# Revit family: Guardrail_Kattsafe_TopMount
name_source: partatom
category: Specialty Equipment
units: mm (PartAtom-declared; Revit-internal decimal feet)

## family parameters
Cut with Voids When Loaded = No
Enable Cutting in Views = No
Maintain Annotation Orientation = No
OmniClass Number = 23.17.25.11
Part Type = Normal
Room Calculation Point = No
Round Connector Dimension = Use Diameter
Shared = No

## types (1)
- Type 1
    Assembly Code = E1090100
    Default Elevation = 0 mm  [stored 0 ft]
    Description = Kattsafe guardrail systems are the preferred method of safe access across roofs and areas close to a fall edge. The system requires no specialist PPE, personnel or training to safely prevent a fall with a walkway to designate a safe path of access across the roof surface.
    Export Type to IFC As = IfcRailing
    GuardrailHeight = 1000 mm  [stored 3.28084 ft]
    HandrailAngledOffsetHeight = -57 mm
    HandrailClosureAngledOffsetHeight = -532 mm
    IfcExportAs = IfcRailing
    IfcExportType = GUARDRAIL
    Manufacturer = Kattsafe®
    ManufacturerOverallHeight = 1000 mm  [stored 3.28084 ft]
    ManufacturerOverallHeightCalc = 1000 mm  [stored 3.28084 ft]
    ManufacturerOverallWidth = 80 mm  [stored 0.262467 ft]
    ManufacturerSpecCode = GW1
    ManufacturerURLProductSpecific = https://kattsafe.com.au
    Material = Aluminum_Kattsafe_Satin
    Model = GW1
    ModifiedIssue = 20240430 $
    PostsHeight = 958 mm  [stored 3.14304 ft]
    PostsMaxSpacingLength = 2000 mm  [stored 6.56168 ft]
    Type Comments = Guardrail - Side Mount
    Type IFC Predefined Type = GUARDRAIL
    URL = https://kattsafe.com.au
    Uniclass2015Code = Pr_25_30_36_03
    Uniclass2015Title = Aluminium handrails
    Uniclass2015Version = Products v1.23

note: [stored X ft] marks values corroborated as IEEE doubles in the binary element streams (Revit-internal decimal feet)

## geometry (parser evidence)
native form markers: Sweep x8
no freeform markers — native parametric forms only
